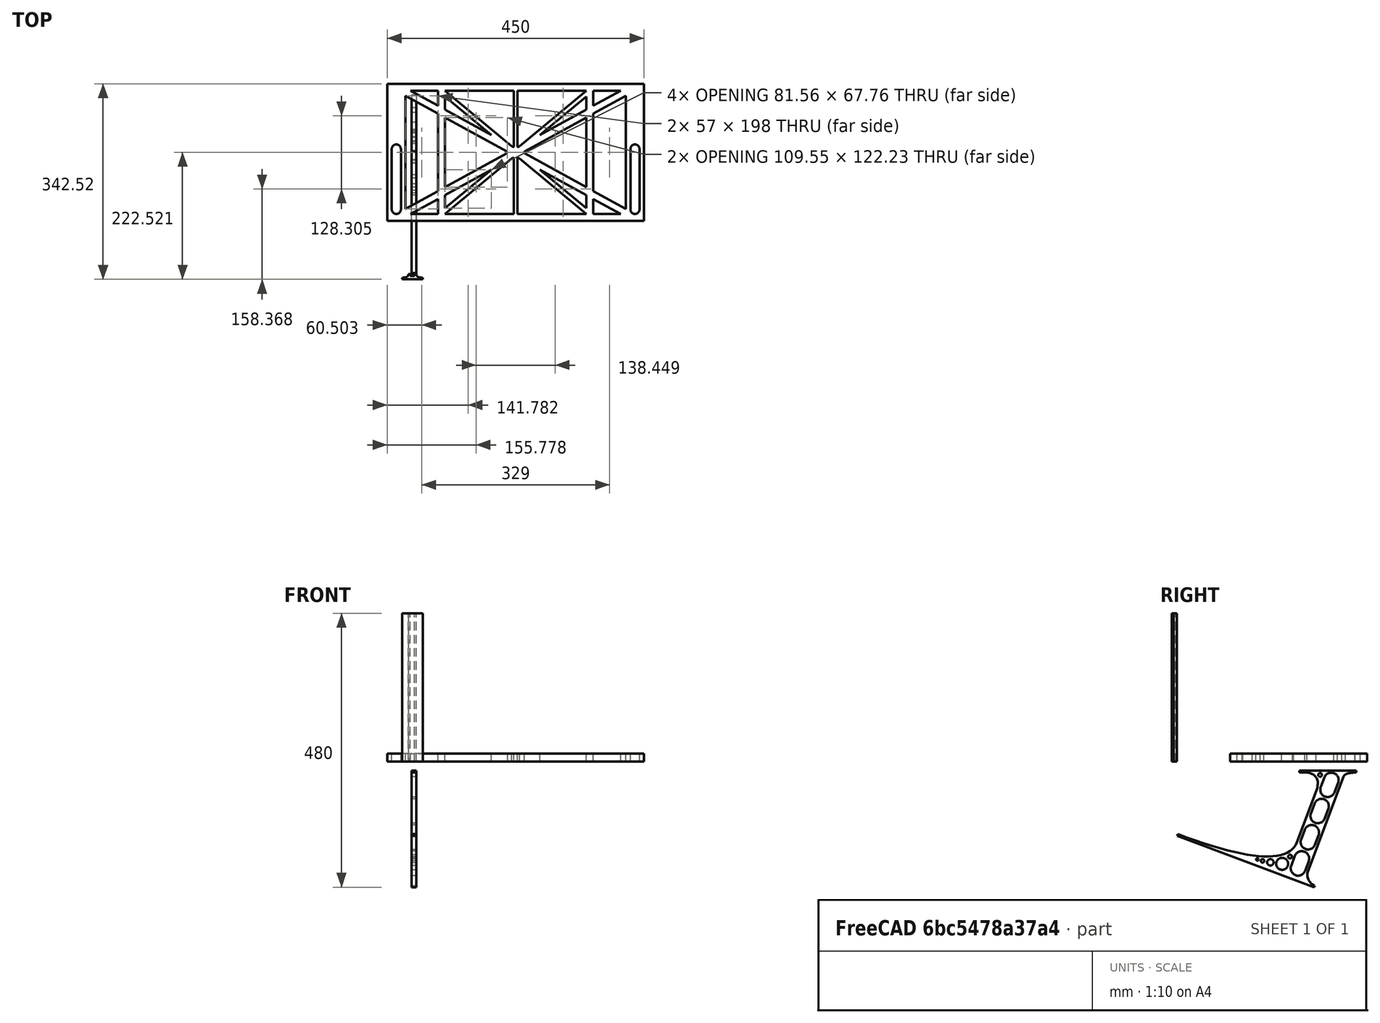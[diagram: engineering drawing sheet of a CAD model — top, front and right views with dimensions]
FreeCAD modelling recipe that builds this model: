
FCSTD DOCUMENT  (FreeCAD 0.19R0.19.2)
Label: laptopStand058
License: All rights reserved
LicenseURL: http://en.wikipedia.org/wiki/All_rights_reserved
objects: Sketcher::SketchObject×3, Part::Extrusion×3
note: 6 computed .brp shape members not serialized (recipe doc carries the construction recipe); baked Part::Feature solids carry a one-line shape summary decoded from their .brp

FEATURE [Sketcher::SketchObject] Sketch
  FullyConstrained = true
  sketch-geometry (100):
    g0: LineSegment StartX=-22.9272 StartY=136.221 StartZ=0 EndX=387.073 EndY=136.221 EndZ=0
    g1: LineSegment StartX=375.073 StartY=115.221 StartZ=0 EndX=318.073 EndY=83.9235 EndZ=0
    g2: LineSegment StartX=-10.9272 StartY=-82.7794 StartZ=0 EndX=46.0728 EndY=-51.4823 EndZ=0
    g3: LineSegment StartX=-1.92718 StartY=124.221 StartZ=0 EndX=46.0728 EndY=97.8651 EndZ=0
    g4: LineSegment StartX=366.073 StartY=-91.7794 StartZ=0 EndX=318.073 EndY=-65.424 EndZ=0
    g5: LineSegment StartX=-10.9272 StartY=115.221 StartZ=0 EndX=-10.9272 EndY=-82.7794 EndZ=0
    g6: LineSegment StartX=375.073 StartY=-82.7794 StartZ=0 EndX=375.073 EndY=115.221 EndZ=0
    g7: LineSegment StartX=-1.92719 StartY=-91.7794 StartZ=0 EndX=46.0728 EndY=-91.7794 EndZ=0
    g8: LineSegment StartX=318.073 StartY=124.221 StartZ=0 EndX=366.073 EndY=124.221 EndZ=0
    g9: LineSegment StartX=306.073 StartY=-81.8102 StartZ=0 EndX=224.513 EndY=-14.0532 EndZ=0
    g10: LineSegment StartX=58.0728 StartY=114.251 StartZ=0 EndX=139.632 EndY=46.4944 EndZ=0
    g11: LineSegment StartX=306.073 StartY=124.221 StartZ=0 EndX=189.124 EndY=27.0628 EndZ=0
    g12: LineSegment StartX=58.0728 StartY=-91.7794 StartZ=0 EndX=175.022 EndY=5.37834 EndZ=0
    g13: LineSegment StartX=46.0728 StartY=124.221 StartZ=0 EndX=46.0728 EndY=97.8651 EndZ=0
    g14: LineSegment StartX=58.0728 StartY=-81.8102 StartZ=0 EndX=58.0728 EndY=-58.8351 EndZ=0
    g15: LineSegment StartX=318.073 StartY=124.221 StartZ=0 EndX=318.073 EndY=97.8651 EndZ=0
    g16: LineSegment StartX=306.073 StartY=114.251 StartZ=0 EndX=306.073 EndY=91.2763 EndZ=0
    g17: LineSegment StartX=224.513 StartY=46.4944 StartZ=0 EndX=306.073 EndY=114.251 EndZ=0
    g18: LineSegment StartX=175.022 StartY=27.0628 StartZ=0 EndX=58.0728 EndY=124.221 EndZ=0
    g19: LineSegment StartX=139.632 StartY=-14.0532 StartZ=0 EndX=58.0728 EndY=-81.8102 EndZ=0
    g20: LineSegment StartX=224.513 StartY=46.4944 StartZ=0 EndX=306.073 EndY=91.2763 EndZ=0
    g21: LineSegment StartX=139.632 StartY=-14.0532 StartZ=0 EndX=58.0728 EndY=-58.8351 EndZ=0
    g22: LineSegment StartX=189.124 StartY=5.37834 StartZ=0 EndX=306.073 EndY=-91.7794 EndZ=0
    g23: LineSegment StartX=306.073 StartY=77.3346 StartZ=0 EndX=306.073 EndY=-44.8935 EndZ=0
    g24: LineSegment StartX=318.073 StartY=83.9235 StartZ=0 EndX=318.073 EndY=-51.4823 EndZ=0
    g25: LineSegment StartX=318.073 StartY=97.8651 StartZ=0 EndX=366.073 EndY=124.221 EndZ=0
    g26: LineSegment StartX=306.073 StartY=-58.8351 StartZ=0 EndX=224.513 EndY=-14.0532 EndZ=0
    g27: LineSegment StartX=306.073 StartY=-58.8351 StartZ=0 EndX=306.073 EndY=-81.8102 EndZ=0
    g28: LineSegment StartX=318.073 StartY=-51.4823 StartZ=0 EndX=375.073 EndY=-82.7794 EndZ=0
    g29: LineSegment StartX=318.073 StartY=-65.424 StartZ=0 EndX=318.073 EndY=-91.7794 EndZ=0
    g30: LineSegment StartX=318.073 StartY=-91.7794 StartZ=0 EndX=366.073 EndY=-91.7794 EndZ=0
    g31: LineSegment StartX=58.0728 StartY=-44.8935 StartZ=0 EndX=58.0728 EndY=77.3346 EndZ=0
    g32: LineSegment StartX=46.0728 StartY=-65.424 StartZ=0 EndX=-1.92719 EndY=-91.7794 EndZ=0
    g33: LineSegment StartX=46.0728 StartY=-65.424 StartZ=0 EndX=46.0728 EndY=-91.7794 EndZ=0
    g34: LineSegment StartX=58.0728 StartY=91.2763 StartZ=0 EndX=58.0728 EndY=114.251 EndZ=0
    g35: LineSegment StartX=46.0728 StartY=83.9235 StartZ=0 EndX=46.0728 EndY=-51.4823 EndZ=0
    g36: LineSegment StartX=46.0728 StartY=124.221 StartZ=0 EndX=-1.92719 EndY=124.221 EndZ=0
    g37: LineSegment StartX=58.0728 StartY=91.2763 StartZ=0 EndX=139.632 EndY=46.4944 EndZ=0
    g38: LineSegment StartX=46.0728 StartY=83.9235 StartZ=0 EndX=-10.9272 EndY=115.221 EndZ=0
    g39: LineSegment StartX=-22.9272 StartY=136.221 StartZ=0 EndX=-42.9272 EndY=136.221 EndZ=0
    g40: LineSegment StartX=387.073 StartY=136.221 StartZ=0 EndX=407.073 EndY=136.221 EndZ=0
    g41: LineSegment StartX=-42.9272 StartY=136.221 StartZ=0 EndX=-42.9272 EndY=-103.779 EndZ=0
    g42: LineSegment StartX=407.073 StartY=136.221 StartZ=0 EndX=407.073 EndY=-103.779 EndZ=0
    g43: LineSegment StartX=179.022 StartY=27.0628 StartZ=0 EndX=179.022 EndY=124.221 EndZ=0
    g44: LineSegment StartX=185.124 StartY=27.0628 StartZ=0 EndX=185.124 EndY=124.221 EndZ=0
    g45: ArcOfCircle CenterX=-26.9272 CenterY=22.1087 CenterZ=0 NormalX=0 NormalY=0 NormalZ=1 AngleXU=0 Radius=8 StartAngle=1e-16 EndAngle=3.14159
    g46: ArcOfCircle CenterX=-26.9272 CenterY=-83.7794 CenterZ=0 NormalX=0 NormalY=0 NormalZ=1 AngleXU=0 Radius=8 StartAngle=3.14159 EndAngle=6.28319
    g47: LineSegment StartX=-34.9272 StartY=22.1087 StartZ=0 EndX=-34.9272 EndY=-83.7794 EndZ=0
    g48: LineSegment StartX=-18.9272 StartY=22.1087 StartZ=0 EndX=-18.9272 EndY=-83.7794 EndZ=0
    g49: LineSegment StartX=185.124 StartY=-91.7794 StartZ=0 EndX=306.073 EndY=-91.7794 EndZ=0
    g50: LineSegment StartX=179.022 StartY=-91.7794 StartZ=0 EndX=58.0728 EndY=-91.7794 EndZ=0
    g51: LineSegment StartX=306.073 StartY=124.221 StartZ=0 EndX=185.124 EndY=124.221 EndZ=0
    g52: LineSegment StartX=179.022 StartY=124.221 StartZ=0 EndX=58.0728 EndY=124.221 EndZ=0
    g53: ArcOfCircle CenterX=391.073 CenterY=22.1087 CenterZ=0 NormalX=0 NormalY=0 NormalZ=1 AngleXU=0 Radius=8 StartAngle=-4.4e-15 EndAngle=3.14159
    g54: LineSegment StartX=399.073 StartY=22.1087 StartZ=0 EndX=399.073 EndY=-83.7794 EndZ=0
    g55: LineSegment StartX=383.073 StartY=22.1087 StartZ=0 EndX=383.073 EndY=-83.7794 EndZ=0
    g56: ArcOfCircle CenterX=391.073 CenterY=-83.7794 CenterZ=0 NormalX=0 NormalY=0 NormalZ=1 AngleXU=0 Radius=8 StartAngle=3.14159 EndAngle=6.28319
    g57: Circle CenterX=175.022 CenterY=27.0628 CenterZ=0 NormalX=0 NormalY=0 NormalZ=1 AngleXU=0 Radius=1
    g58: Circle CenterX=179.022 CenterY=24.8665 CenterZ=0 NormalX=0 NormalY=0 NormalZ=1 AngleXU=0 Radius=1
    g59: Circle CenterX=179.022 CenterY=27.0628 CenterZ=0 NormalX=0 NormalY=0 NormalZ=1 AngleXU=0 Radius=1
    g60: BSplineCurve PolesCount=3 KnotsCount=2 Degree=2 IsPeriodic=0
    g61: GeomPoint X=175.022 Y=27.0628 Z=0
    g62: GeomPoint X=179.022 Y=27.0628 Z=0
    g63: Circle CenterX=189.124 CenterY=27.0628 CenterZ=0 NormalX=0 NormalY=0 NormalZ=1 AngleXU=0 Radius=1
    g64: Circle CenterX=185.124 CenterY=24.8665 CenterZ=0 NormalX=0 NormalY=0 NormalZ=1 AngleXU=0 Radius=1
    g65: Circle CenterX=185.124 CenterY=27.0628 CenterZ=0 NormalX=0 NormalY=0 NormalZ=1 AngleXU=0 Radius=1
    g66: BSplineCurve PolesCount=3 KnotsCount=2 Degree=2 IsPeriodic=0
    g67: GeomPoint X=189.124 Y=27.0628 Z=0
    g68: GeomPoint X=185.124 Y=27.0628 Z=0
    g69: Circle CenterX=175.022 CenterY=5.37834 CenterZ=0 NormalX=0 NormalY=0 NormalZ=1 AngleXU=0 Radius=1
    g70: Circle CenterX=179.022 CenterY=7.57463 CenterZ=0 NormalX=0 NormalY=0 NormalZ=1 AngleXU=0 Radius=1
    g71: Circle CenterX=179.022 CenterY=5.34704 CenterZ=0 NormalX=0 NormalY=0 NormalZ=1 AngleXU=0 Radius=1
    g72: BSplineCurve PolesCount=3 KnotsCount=2 Degree=2 IsPeriodic=0
    g73: GeomPoint X=175.022 Y=5.37834 Z=0
    g74: GeomPoint X=179.022 Y=5.34704 Z=0
    g75: Circle CenterX=189.124 CenterY=5.37834 CenterZ=0 NormalX=0 NormalY=0 NormalZ=1 AngleXU=0 Radius=1
    g76: Circle CenterX=185.124 CenterY=7.57463 CenterZ=0 NormalX=0 NormalY=0 NormalZ=1 AngleXU=0 Radius=1
    g77: Circle CenterX=185.124 CenterY=5.34704 CenterZ=0 NormalX=0 NormalY=0 NormalZ=1 AngleXU=0 Radius=1
    g78: BSplineCurve PolesCount=3 KnotsCount=2 Degree=2 IsPeriodic=0
    g79: GeomPoint X=189.124 Y=5.37834 Z=0
    g80: GeomPoint X=185.124 Y=5.34704 Z=0
    g81: LineSegment StartX=179.022 StartY=5.34704 StartZ=0 EndX=179.022 EndY=-91.7794 EndZ=0
    g82: LineSegment StartX=185.124 StartY=-91.7794 StartZ=0 EndX=185.124 EndY=5.34704 EndZ=0
    g83: Circle CenterX=165.871 CenterY=18.1458 CenterZ=0 NormalX=0 NormalY=0 NormalZ=1 AngleXU=0 Radius=1
    g84: Circle CenterX=169.377 CenterY=16.2206 CenterZ=0 NormalX=0 NormalY=0 NormalZ=1 AngleXU=0 Radius=1
    g85: Circle CenterX=165.871 CenterY=14.2954 CenterZ=0 NormalX=0 NormalY=0 NormalZ=1 AngleXU=0 Radius=1
    g86: BSplineCurve PolesCount=3 KnotsCount=2 Degree=2 IsPeriodic=0
    g87: GeomPoint X=165.871 Y=18.1458 Z=0
    g88: GeomPoint X=165.871 Y=14.2954 Z=0
    g89: Circle CenterX=198.275 CenterY=18.1458 CenterZ=0 NormalX=0 NormalY=0 NormalZ=1 AngleXU=0 Radius=1
    g90: Circle CenterX=194.768 CenterY=16.2206 CenterZ=0 NormalX=0 NormalY=0 NormalZ=1 AngleXU=0 Radius=1
    g91: Circle CenterX=198.275 CenterY=14.2954 CenterZ=0 NormalX=0 NormalY=0 NormalZ=1 AngleXU=0 Radius=1
    g92: BSplineCurve PolesCount=3 KnotsCount=2 Degree=2 IsPeriodic=0
    g93: GeomPoint X=198.275 Y=18.1458 Z=0
    g94: GeomPoint X=198.275 Y=14.2954 Z=0
    g95: LineSegment StartX=165.871 StartY=18.1458 StartZ=0 EndX=58.0728 EndY=77.3346 EndZ=0
    g96: LineSegment StartX=58.0728 StartY=-44.8935 StartZ=0 EndX=165.871 EndY=14.2954 EndZ=0
    g97: LineSegment StartX=198.275 StartY=18.1458 StartZ=0 EndX=306.073 EndY=77.3346 EndZ=0
    g98: LineSegment StartX=198.275 StartY=14.2954 StartZ=0 EndX=306.073 EndY=-44.8935 EndZ=0
    g99: LineSegment StartX=407.073 StartY=-103.779 StartZ=0 EndX=-42.9272 EndY=-103.779 EndZ=0
  constraints (189):
    c: Horizontal(g0)
    c: Distance(g0) = 410
    c: Block(g0)
    c: Horizontal(g7)
    c: Horizontal(g8)
    c: Coincident(g37,g10)
    c: Coincident(g17,g20)
    c: Coincident(g21,g19)
    c: Coincident(g26,g9)
    c: Coincident(g17,g16)
    c: Tangent(g16,g23)
    c: Tangent(g15,g24)
    c: Coincident(g20,g16)
    c: Tangent(g20,g25)
    c: Coincident(g1,g24)
    c: Coincident(g27,g9)
    c: Tangent(g4,g26)
    c: Tangent(g23,g27)
    c: Coincident(g24,g28)
    c: Coincident(g29,g4)
    c: Tangent(g24,g29)
    c: Coincident(g19,g14)
    c: Tangent(g14,g31)
    c: Coincident(g21,g14)
    c: Tangent(g21,g32)
    c: Coincident(g33,g32)
    c: Tangent(g13,g33)
    c: Coincident(g2,g35)
    c: Tangent(g31,g34)
    c: Tangent(g13,g35)
    c: Coincident(g10,g34)
    c: Coincident(g3,g13)
    c: Coincident(g37,g34)
    c: Tangent(g3,g37)
    c: Coincident(g38,g35)
    c: Block(g18)
    c: Block(g11)
    c: Block(g15)
    c: Block(g25)
    c: Block(g1)
    c: Block(g28)
    c: Block(g6)
    c: Block(g26)
    c: Block(g27)
    c: Block(g4)
    c: Block(g29)
    c: Block(g17)
    c: Block(g22)
    c: Block(g12)
    c: Block(g21)
    c: Block(g19)
    c: Block(g33)
    c: Block(g32)
    c: Block(g2)
    c: Block(g5)
    c: Block(g38)
    c: Block(g3)
    c: Block(g13)
    c: Block(g10)
    c: Block(g34)
    c: Block(g23)
    c: Block(g36)
    c: Block(g8)
    c: Block(g30)
    c: Block(g7)
    c: Horizontal(g39)
    c: Distance(g39) = 20
    c: Coincident(g40,g0)
    c: Horizontal(g40)
    c: Distance(g40) = 20
    c: Coincident(g41,g39)
    c: Vertical(g41)
    c: Coincident(g42,g40)
    c: Vertical(g42)
    c: Block(g42)
    c: Block(g41)
    c: Vertical(g43)
    c: Vertical(g44)
    c: Block(g43)
    c: Block(g44)
    c: Tangent(g45,g48) = 1.5708
    c: Tangent(g45,g47) = -1.5708
    c: Tangent(g47,g46) = -1.5708
    c: Tangent(g48,g46) = 1.5708
    c: Vertical(g47)
    c: Equal(g45,g46)
    c: Block(g48)
    c: Block(g47)
    c: Coincident(g49,g22)
    c: Horizontal(g49)
    c: Coincident(g50,g12)
    c: Horizontal(g50)
    c: Coincident(g51,g11)
    c: Coincident(g51,g44)
    c: Horizontal(g51)
    c: Coincident(g52,g43)
    c: Coincident(g52,g18)
    c: Horizontal(g52)
    c: Tangent(g53,g54) = 1.5708
    c: Tangent(g54,g56) = 1.5708
    c: Equal(g53,g56)
    c: Coincident(g55,g53)
    c: Coincident(g55,g56)
    c: Block(g54)
    c: Block(g55)
    c: Coincident(g60,g18)
    c: Weight(g57) = 1
    c: Equal(g57,g58)
    c: Equal(g57,g59)
    c: Coincident(g60,g43)
    c: InternalAlignment(g57,g60)
    c: InternalAlignment(g58,g60)
    c: InternalAlignment(g59,g60)
    c: InternalAlignment(g61,g60)
    c: InternalAlignment(g62,g60)
    c: Coincident(g66,g11)
    c: Weight(g63) = 1
    c: Equal(g63,g64)
    c: Equal(g63,g65)
    c: Coincident(g66,g44)
    c: InternalAlignment(g63,g66)
    c: InternalAlignment(g64,g66)
    c: InternalAlignment(g65,g66)
    c: InternalAlignment(g67,g66)
    c: InternalAlignment(g68,g66)
    c: Block(g66)
    c: Block(g60)
    c: Coincident(g72,g12)
    c: Weight(g69) = 1
    c: Equal(g69,g70)
    c: Equal(g69,g71)
    c: InternalAlignment(g69,g72)
    c: InternalAlignment(g70,g72)
    c: InternalAlignment(g71,g72)
    c: InternalAlignment(g73,g72)
    c: InternalAlignment(g74,g72)
    c: Weight(g75) = 1
    c: Equal(g75,g76)
    c: Equal(g75,g77)
    c: InternalAlignment(g75,g78)
    c: InternalAlignment(g76,g78)
    c: InternalAlignment(g77,g78)
    c: InternalAlignment(g79,g78)
    c: InternalAlignment(g80,g78)
    c: Block(g78)
    c: Block(g72)
    c: Coincident(g81,g72)
    c: Coincident(g81,g50)
    c: Vertical(g81)
    c: Coincident(g82,g49)
    c: Coincident(g82,g78)
    c: Vertical(g82)
    c: Weight(g83) = 1
    c: Equal(g83,g84)
    c: Equal(g83,g85)
    c: InternalAlignment(g83,g86)
    c: InternalAlignment(g84,g86)
    c: InternalAlignment(g85,g86)
    c: InternalAlignment(g87,g86)
    c: InternalAlignment(g88,g86)
    c: Weight(g89) = 1
    c: Equal(g89,g90)
    c: Equal(g89,g91)
    c: InternalAlignment(g89,g92)
    c: InternalAlignment(g90,g92)
    c: InternalAlignment(g91,g92)
    c: InternalAlignment(g93,g92)
    c: InternalAlignment(g94,g92)
    c: Block(g86)
    c: Block(g92)
    c: Coincident(g95,g86)
    c: Coincident(g95,g31)
    c: Coincident(g96,g31)
    c: Coincident(g96,g86)
    c: Coincident(g97,g92)
    c: Coincident(g97,g23)
    c: Coincident(g98,g92)
    c: Coincident(g98,g23)
    c: Block(g31)
    c: Coincident(g99,g42)
    c: Coincident(g99,g41)
    c: Horizontal(g99)
    c: Distance(g99) = 450
    c: Distance(g0) = 410
    c: Distance(g0) = 410
    c: Distance(g0) = 410
    c: Distance(g0) = 410
    c: Distance(g0) = 410
    c: Distance(g0) = 410
FEATURE [Sketcher::SketchObject] Sketch001
  FullyConstrained = true
  MapMode = 4
  Placement = pos=(0,0,0) rot=(0.57735,0.57735,0.57735;2.0944rad)
  Support = -> [Sketch]
  sketch-geometry (46):
    g0: BSplineCurve PolesCount=3 KnotsCount=2 Degree=2 IsPeriodic=0
    g1: ArcOfCircle CenterX=73.122 CenterY=-32.2909 CenterZ=0 NormalX=0 NormalY=0 NormalZ=1 AngleXU=0 Radius=13 StartAngle=5.92268 EndAngle=9.06428
    g2: ArcOfCircle CenterX=66.7816 CenterY=-49.1439 CenterZ=0 NormalX=0 NormalY=0 NormalZ=1 AngleXU=0 Radius=13 StartAngle=2.78068 EndAngle=5.92131
    g3: ArcOfCircle CenterX=55.9263 CenterY=-78.1807 CenterZ=0 NormalX=0 NormalY=0 NormalZ=1 AngleXU=0 Radius=13 StartAngle=5.92268 EndAngle=9.06428
    g4: ArcOfCircle CenterX=49.5884 CenterY=-95.0342 CenterZ=0 NormalX=0 NormalY=0 NormalZ=1 AngleXU=0 Radius=13 StartAngle=2.78068 EndAngle=5.92131
    g5: ArcOfCircle CenterX=38.7206 CenterY=-124.067 CenterZ=0 NormalX=0 NormalY=0 NormalZ=1 AngleXU=0 Radius=13 StartAngle=5.92268 EndAngle=9.06428
    g6: ArcOfCircle CenterX=32.3875 CenterY=-140.92 CenterZ=0 NormalX=0 NormalY=0 NormalZ=1 AngleXU=0 Radius=13 StartAngle=2.78068 EndAngle=5.92131
    g7: ArcOfCircle CenterX=21.4715 CenterY=-169.934 CenterZ=0 NormalX=0 NormalY=0 NormalZ=1 AngleXU=0 Radius=13 StartAngle=5.92268 EndAngle=9.06428
    g8: ArcOfCircle CenterX=15.1336 CenterY=-186.787 CenterZ=0 NormalX=0 NormalY=0 NormalZ=1 AngleXU=0 Radius=13 StartAngle=2.78068 EndAngle=5.92131
    g9-g12: Circle x4 (B-spline internal-alignment scaffolding for g13; pole/knot coordinates omitted)
    g13: BSplineCurve PolesCount=4 KnotsCount=2 Degree=3 IsPeriodic=0
    g14: GeomPoint X=28.8094 Y=-19.0875 Z=0
    g15: GeomPoint X=47.0443 Y=-50.4712 Z=0
    g16: Circle CenterX=53.5586 CenterY=-23.2695 CenterZ=0 NormalX=0 NormalY=0 NormalZ=1 AngleXU=0 Radius=3.24518
    g17: Circle CenterX=-195.441 CenterY=-127.082 CenterZ=0 NormalX=0 NormalY=0 NormalZ=1 AngleXU=0 Radius=1
    g18: Circle CenterX=-8.24091 CenterY=-197.481 CenterZ=0 NormalX=0 NormalY=0 NormalZ=1 AngleXU=0 Radius=1
    g19: Circle CenterX=12.8789 CenterY=-141.321 CenterZ=0 NormalX=0 NormalY=0 NormalZ=1 AngleXU=0 Radius=1
    g20: BSplineCurve PolesCount=3 KnotsCount=2 Degree=2 IsPeriodic=0
    g21: GeomPoint X=-195.441 Y=-127.082 Z=0
    g22: GeomPoint X=12.8789 Y=-141.321 Z=0
    g23: Circle CenterX=-12.8016 CenterY=-179.036 CenterZ=0 NormalX=0 NormalY=0 NormalZ=1 AngleXU=0 Radius=10.5072
    g24: Circle CenterX=0.933922 CenterY=-166.43 CenterZ=0 NormalX=0 NormalY=0 NormalZ=1 AngleXU=0 Radius=3.26661
    g25: Circle CenterX=-33.5518 CenterY=-176.44 CenterZ=0 NormalX=0 NormalY=0 NormalZ=1 AngleXU=0 Radius=5.64388
    g26: Circle CenterX=-47.2366 CenterY=-173.859 CenterZ=0 NormalX=0 NormalY=0 NormalZ=1 AngleXU=0 Radius=3.01653
    g27: Circle CenterX=-56.2595 CenterY=-171.456 CenterZ=0 NormalX=0 NormalY=0 NormalZ=1 AngleXU=0 Radius=2.12826
    g28: ArcOfCircle CenterX=51.2151 CenterY=-198.473 CenterZ=0 NormalX=0 NormalY=0 NormalZ=1 AngleXU=0 Radius=20 StartAngle=2.78189 EndAngle=4.35269
    g29: LineSegment StartX=32.4951 StartY=-191.433 StartZ=0 EndX=94.6577 EndY=-26.1351 EndZ=0
    g30: LineSegment StartX=43.1192 StartY=-220.001 StartZ=0 EndX=-196.497 EndY=-129.89 EndZ=0
    g31: LineSegment StartX=43.1192 StartY=-220.001 StartZ=0 EndX=44.1752 EndY=-217.193 EndZ=0
    g32: LineSegment StartX=117.223 StartY=-19.0875 StartZ=0 EndX=117.223 EndY=-16.0875 EndZ=0
    g33: LineSegment StartX=117.223 StartY=-16.0875 StartZ=0 EndX=17.2232 EndY=-16.0875 EndZ=0
    g34: LineSegment StartX=17.2232 StartY=-16.0875 StartZ=0 EndX=17.2232 EndY=-19.0875 EndZ=0
    g35: LineSegment StartX=28.8094 StartY=-19.0875 StartZ=0 EndX=17.2232 EndY=-19.0875 EndZ=0
    g36: LineSegment StartX=47.0443 StartY=-50.4712 StartZ=0 EndX=12.8789 EndY=-141.321 EndZ=0
    g37: LineSegment StartX=-195.441 StartY=-127.082 StartZ=0 EndX=-196.497 EndY=-129.89 EndZ=0
    g38: LineSegment StartX=85.2864 StartY=-36.8765 StartZ=0 EndX=78.9396 EndY=-53.7463 EndZ=0
    g39: LineSegment StartX=60.9577 StartY=-27.7052 StartZ=0 EndX=54.6191 EndY=-44.5532 EndZ=0
    g40: LineSegment StartX=68.0907 StartY=-82.7664 StartZ=0 EndX=61.7465 EndY=-99.6365 EndZ=0
    g41: LineSegment StartX=43.7619 StartY=-73.595 StartZ=0 EndX=37.426 EndY=-90.4435 EndZ=0
    g42: LineSegment StartX=50.885 StartY=-128.652 StartZ=0 EndX=44.5456 EndY=-145.522 EndZ=0
    g43: LineSegment StartX=26.5562 StartY=-119.481 StartZ=0 EndX=20.2251 EndY=-136.329 EndZ=0
    g44: LineSegment StartX=9.3071 StartY=-165.349 StartZ=0 EndX=2.97115 EndY=-182.197 EndZ=0
    g45: LineSegment StartX=33.6358 StartY=-174.52 StartZ=0 EndX=27.2917 EndY=-191.39 EndZ=0
  constraints (70):
    c: Block(g0)
    c: Block(g1)
    c: Block(g2)
    c: Block(g4)
    c: Block(g3)
    c: Block(g6)
    c: Block(g5)
    c: Block(g8)
    c: Block(g7)
    c: Weight(g9) = 1
    c: Equal(g9,g10)
    c: Equal(g9,g11)
    c: Equal(g9,g12)
    c: InternalAlignment(g9-g12 -> g13) x4
    c: InternalAlignment(g14,g13)
    c: InternalAlignment(g15,g13)
    c: Block(g16)
    c: Weight(g17) = 1
    c: Equal(g17,g18)
    c: Equal(g17,g19)
    c: InternalAlignment(g17,g20)
    c: InternalAlignment(g18,g20)
    c: InternalAlignment(g19,g20)
    c: InternalAlignment(g21,g20)
    c: InternalAlignment(g22,g20)
    c: Block(g20)
    c: Block(g23)
    c: Block(g24)
    c: Block(g25)
    c: Block(g26)
    c: Block(g27)
    c: Block(g28)
    c: Coincident(g29,g28)
    c: Coincident(g29,g0)
    c: Block(g13)
    c: Coincident(g31,g30)
    c: Coincident(g31,g28)
    c: Block(g31)
    c: Coincident(g32,g0)
    c: Vertical(g32)
    c: Coincident(g33,g32)
    c: Horizontal(g33)
    c: Coincident(g34,g33)
    c: Vertical(g34)
    c: Block(g33)
    c: Coincident(g35,g13)
    c: Coincident(g35,g34)
    c: Horizontal(g35)
    c: Coincident(g36,g13)
    c: Coincident(g36,g20)
    c: Coincident(g37,g20)
    c: Coincident(g37,g30)
    c: Block(g30)
    c: Coincident(g38,g1)
    c: Coincident(g38,g2)
    c: Coincident(g39,g1)
    c: Coincident(g39,g2)
    c: Coincident(g40,g3)
    c: Coincident(g40,g4)
    c: Coincident(g41,g3)
    c: Coincident(g41,g4)
    c: Coincident(g42,g5)
    c: Coincident(g42,g6)
    c: Coincident(g43,g5)
    c: Coincident(g43,g6)
    c: Coincident(g44,g7)
    c: Coincident(g44,g8)
    c: Coincident(g45,g7)
    c: Coincident(g45,g8)
    c: Distance(g30) = 256
FEATURE [Part::Extrusion] Extrude002
  Base = -> Sketch001
  Dir = (1,0,0)
  DirMode = 2
  FaceMakerClass = Part::FaceMakerBullseye
  LengthFwd = 8
  LengthRev = 0
  Solid = true
  Symmetric = false
FEATURE [Sketcher::SketchObject] Sketch002
  FullyConstrained = true
  sketch-geometry (20):
    g0: LineSegment StartX=-2.77179 StartY=-200.304 StartZ=0 EndX=5.22821 EndY=-200.304 EndZ=0
    g1: LineSegment StartX=5.22821 StartY=-200.304 StartZ=0 EndX=5.22821 EndY=-197.304 EndZ=0
    g2: LineSegment StartX=-2.77179 StartY=-200.304 StartZ=0 EndX=-2.77179 EndY=-197.304 EndZ=0
    g3: LineSegment StartX=5.22821 StartY=-197.304 StartZ=0 EndX=8.22821 EndY=-197.304 EndZ=0
    g4: LineSegment StartX=-2.77179 StartY=-197.304 StartZ=0 EndX=-5.77179 EndY=-197.304 EndZ=0
    g5: LineSegment StartX=19.2282 StartY=-203.304 StartZ=0 EndX=19.2282 EndY=-206.304 EndZ=0
    g6: LineSegment StartX=-16.7718 StartY=-203.304 StartZ=0 EndX=-16.7718 EndY=-206.304 EndZ=0
    g7: LineSegment StartX=-16.7718 StartY=-206.304 StartZ=0 EndX=19.2282 EndY=-206.304 EndZ=0
    g8: Circle CenterX=-16.7718 CenterY=-203.304 CenterZ=0 NormalX=0 NormalY=0 NormalZ=1 AngleXU=0 Radius=1
    g9: Circle CenterX=-5.77179 CenterY=-203.304 CenterZ=0 NormalX=0 NormalY=0 NormalZ=1 AngleXU=0 Radius=1
    g10: Circle CenterX=-5.77179 CenterY=-197.304 CenterZ=0 NormalX=0 NormalY=0 NormalZ=1 AngleXU=0 Radius=1
    g11: BSplineCurve PolesCount=3 KnotsCount=2 Degree=2 IsPeriodic=0
    g12: GeomPoint X=-16.7718 Y=-203.304 Z=0
    g13: GeomPoint X=-5.77179 Y=-197.304 Z=0
    g14: Circle CenterX=19.2282 CenterY=-203.304 CenterZ=0 NormalX=0 NormalY=0 NormalZ=1 AngleXU=0 Radius=1
    g15: Circle CenterX=8.22821 CenterY=-203.304 CenterZ=0 NormalX=0 NormalY=0 NormalZ=1 AngleXU=0 Radius=1
    g16: Circle CenterX=8.22821 CenterY=-197.304 CenterZ=0 NormalX=0 NormalY=0 NormalZ=1 AngleXU=0 Radius=1
    g17: BSplineCurve PolesCount=3 KnotsCount=2 Degree=2 IsPeriodic=0
    g18: GeomPoint X=19.2282 Y=-203.304 Z=0
    g19: GeomPoint X=8.22821 Y=-197.304 Z=0
  constraints (41):
    c: Horizontal(g0)
    c: Distance(g0) = 8
    c: Coincident(g1,g0)
    c: Vertical(g1)
    c: Distance(g1) = 3
    c: Coincident(g2,g0)
    c: Vertical(g2)
    c: Distance(g2) = 3
    c: Coincident(g3,g1)
    c: Horizontal(g3)
    c: Distance(g3) = 3
    c: Coincident(g4,g2)
    c: Horizontal(g4)
    c: Distance(g4) = 3
    c: Vertical(g5)
    c: Vertical(g6)
    c: Coincident(g7,g6)
    c: Coincident(g7,g5)
    c: Weight(g8) = 1
    c: Equal(g8,g9)
    c: Equal(g8,g10)
    c: Coincident(g11,g4)
    c: InternalAlignment(g8,g11)
    c: InternalAlignment(g9,g11)
    c: InternalAlignment(g10,g11)
    c: InternalAlignment(g12,g11)
    c: InternalAlignment(g13,g11)
    c: Coincident(g17,g5)
    c: Weight(g14) = 1
    c: Equal(g14,g15)
    c: Equal(g14,g16)
    c: Coincident(g17,g3)
    c: InternalAlignment(g14,g17)
    c: InternalAlignment(g15,g17)
    c: InternalAlignment(g16,g17)
    c: InternalAlignment(g18,g17)
    c: InternalAlignment(g19,g17)
    c: Block(g7)
    c: Block(g17)
    c: Block(g11)
    c: Block(g6)
FEATURE [Part::Extrusion] Extrude003
  Base = -> Sketch002
  Dir = (0,0,1)
  DirMode = 2
  FaceMakerClass = Part::FaceMakerBullseye
  LengthFwd = 260
  LengthRev = 0
  Solid = true
  Symmetric = false
FEATURE [Part::Extrusion] Extrude
  Base = -> Sketch
  Dir = (0,0,1)
  DirMode = 2
  FaceMakerClass = Part::FaceMakerBullseye
  LengthFwd = 14
  LengthRev = 0
  Solid = true
  Symmetric = false
